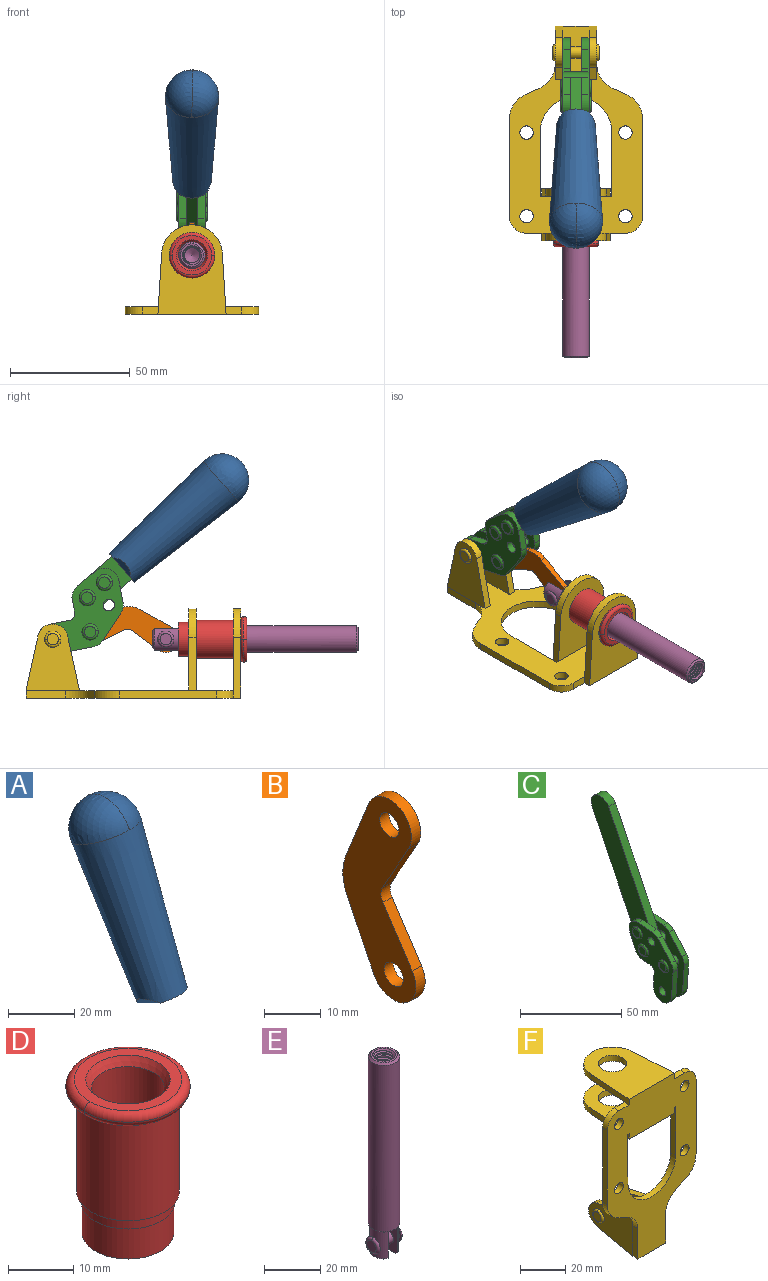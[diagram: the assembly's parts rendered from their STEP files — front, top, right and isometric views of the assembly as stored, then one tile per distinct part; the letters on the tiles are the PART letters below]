
ASSEMBLY  parts=6 mates=6
PART A: 11 faces, bbox 22.3x42.6x64.5 mm
  f0: sphere r=11.13mm, area 411.4mm2, adj f1,f8
  f1: cone r=11.11mm half-angle=3.3deg, axis (0,0.44,0.9), area 3251.8mm2, adj f0,f7,f8,f9,f10
  f2: cylinder r=6.16mm len=11.7mm, axis (1,0,0), area 89.5mm2, adj f3,f4,f5,f6
  f3: plane 60.23x36.75mm, normal (-1,0,0), area 763.6mm2, adj f2,f4,f6,f10
  f4: plane 51.37x25.05mm, normal (0,0.9,-0.44), area 264.2mm2, adj f2,f3,f5,f10
  f5: plane 60.23x36.75mm, normal (1,0,0), area 763.6mm2, adj f2,f4,f6,f10
  f6: plane 51.37x25.05mm, normal (0,-0.9,0.44), area 264.2mm2, adj f2,f3,f5,f10
  f7: plane 9.95x5.95mm, normal (0.71,-0.31,-0.64), area 25.8mm2, adj f1,f10
  f8: sphere r=11.13mm, area 411.4mm2, adj f0,f1
  f9: plane 9.95x5.95mm, normal (-0.71,-0.31,-0.64), area 25.8mm2, adj f1,f10
  f10: plane 14.27x11.38mm, normal (0,-0.44,-0.9), area 106.7mm2, adj f1,f3,f4,f5,f6,f7,f9
PART B: 12 faces, bbox 2.3x18.2x42.8 mm
  f0: cylinder r=2.4mm len=4.8mm, axis (1,0,0), area 34.9mm2, adj f4,f11
  f1: cylinder r=10.41mm len=8.47mm, axis (1,0,0), area 20.2mm2, adj f4,f9,f10,f11
  f2: cylinder r=3.05mm len=3.16mm, axis (1,0,0), area 7.7mm2, adj f4,f6,f7,f11
  f3: cylinder r=2.4mm len=4.8mm, axis (1,0,0), area 34.9mm2, adj f4,f11
  f4: plane 42.81x18.23mm, normal (-1,0,0), area 414.1mm2, adj f0,f1,f2,f3,f5,f6,f7,f8
  f5: cylinder r=5.54mm len=10.67mm, axis (1,0,0), area 41.8mm2, adj f4,f6,f10,f11
  f6: plane 11.66x6.53mm, normal (0,-0.87,-0.49), area 30.9mm2, adj f2,f4,f5,f11
  f7: plane 11.17x7.33mm, normal (0,-0.84,0.55), area 30.9mm2, adj f2,f4,f8,f11
  f8: cylinder r=5.54mm len=10.51mm, axis (1,0,0), area 41.8mm2, adj f4,f7,f9,f11
  f9: plane 13.67x6.67mm, normal (0,0.9,-0.44), area 35.1mm2, adj f1,f4,f8,f11
  f10: plane 14.1x5.7mm, normal (0,0.93,0.37), area 35.1mm2, adj f1,f4,f5,f11
  f11: plane 42.81x18.23mm, normal (1,0,0), area 414.1mm2, adj f0,f1,f2,f3,f5,f6,f7,f8
PART C: 59 faces, bbox 12.9x60.2x99.6 mm
  f0: torus R=2.39mm, axis (-1,0,0), area 14.9mm2, adj f20,f43,f51
  f1: torus R=2.39mm, axis (-1,0,0), area 14.9mm2, adj f19,f42,f51
  f2: torus R=2.39mm, axis (-1,0,0), area 14.9mm2, adj f18,f35,f51
  f3: torus R=2.39mm, axis (-1,0,0), area 14.9mm2, adj f14,f17,f23
  f4: torus R=2.39mm, axis (-1,0,0), area 14.9mm2, adj f13,f16,f23
  f5: torus R=2.39mm, axis (-1,0,0), area 14.9mm2, adj f12,f15,f23
  f6: cylinder r=2.39mm len=4.78mm, axis (1,0,0), area 46.5mm2, adj f48,f50,f51
  f7: cylinder r=2.39mm len=4.78mm, axis (1,0,0), area 46.5mm2, adj f50,f51
  f8: cylinder r=6.35mm len=12.68mm, axis (1,0,0), area 61.8mm2, adj f38,f39,f50,f51
  f9: cylinder r=2.39mm len=4.78mm, axis (-1,0,0), area 70.5mm2, adj f46,f50
  f10: cylinder r=2.39mm len=4.78mm, axis (-1,0,0), area 46.5mm2, adj f23,f45,f46
  f11: cylinder r=2.39mm len=4.78mm, axis (-1,0,0), area 46.5mm2, adj f23,f46
  f12: plane 4.78x4.78mm, normal (1,0,0), area 17.9mm2, adj f5,f15
  f13: plane 4.78x4.78mm, normal (1,0,0), area 17.9mm2, adj f4,f16
  f14: plane 4.78x4.78mm, normal (1,0,0), area 17.9mm2, adj f3,f17
  f15: torus R=2.39mm, axis (-1,0,0), area 14.9mm2, adj f5,f12,f23
  f16: torus R=2.39mm, axis (-1,0,0), area 14.9mm2, adj f4,f13,f23
  f17: torus R=2.39mm, axis (-1,0,0), area 14.9mm2, adj f3,f14,f23
  f18: plane 4.78x4.78mm, normal (-1,0,0), area 17.9mm2, adj f2,f35
  f19: plane 4.78x4.78mm, normal (-1,0,0), area 17.9mm2, adj f1,f42
  f20: plane 4.78x4.78mm, normal (-1,0,0), area 17.9mm2, adj f0,f43
  f21: plane 2.26x0.2mm, normal (1,0,0), area 0.2mm2, adj f31,f44
  f22: plane 2.26x0.2mm, normal (-1,0,0), area 0.2mm2, adj f41,f44
  f23: plane 39.37x30.77mm, normal (1,0,0), area 565.5mm2, adj f3,f4,f5,f10,f11,f15,f16,f17
  f24: cylinder r=6.1mm len=4.15mm, axis (-1,0,0), area 14.7mm2, adj f23,f25,f32,f46
  f25: plane 10.25x9.01mm, normal (0,-0.75,0.66), area 42.3mm2, adj f23,f24,f26,f46
  f26: cylinder r=6.35mm len=4.64mm, axis (-1,0,0), area 15.6mm2, adj f23,f25,f27,f46
  f27: plane 15.84x3.1mm, normal (0,-1,-0.07), area 49.2mm2, adj f23,f26,f28,f46
  f28: cylinder r=6.35mm len=12.68mm, axis (-1,0,0), area 61.8mm2, adj f23,f27,f29,f46
  f29: plane 8.11x3.1mm, normal (0,1,0.07), area 25.2mm2, adj f23,f28,f30,f46
  f30: cylinder r=3.05mm len=3.25mm, axis (-1,0,0), area 14.8mm2, adj f23,f29,f31,f46
  f31: plane 5.99x3.1mm, normal (0,0.07,-1), area 18.6mm2, adj f21,f23,f30,f44,f46
  f32: plane 9.5x3.1mm, normal (0,-0.07,1), area 29.5mm2, adj f23,f24,f33,f46,f47
  f33: cylinder r=6.1mm len=8.63mm, axis (-1,0,0), area 39.1mm2, adj f23,f32,f34,f47
  f34: plane 8.65x3.96mm, normal (0,0.91,-0.42), area 29.5mm2, adj f23,f33,f44,f47
  f35: torus R=2.39mm, axis (-1,0,0), area 14.9mm2, adj f2,f18,f51
  f36: plane 10.25x9.01mm, normal (0,-0.75,0.66), area 42.3mm2, adj f37,f49,f50,f51
  f37: cylinder r=6.35mm len=4.64mm, axis (1,0,0), area 15.6mm2, adj f36,f38,f50,f51
  f38: plane 15.84x3.1mm, normal (0,-1,-0.07), area 49.2mm2, adj f8,f37,f50,f51
  f39: plane 8.11x3.1mm, normal (0,1,0.07), area 25.2mm2, adj f8,f40,f50,f51
  f40: cylinder r=3.05mm len=3.25mm, axis (1,0,0), area 14.8mm2, adj f39,f41,f50,f51
  f41: plane 5.99x3.1mm, normal (0,0.07,-1), area 18.6mm2, adj f22,f40,f44,f50,f51
  f42: torus R=2.39mm, axis (-1,0,0), area 14.9mm2, adj f1,f19,f51
  f43: torus R=2.39mm, axis (-1,0,0), area 14.9mm2, adj f0,f20,f51
  f44: cylinder r=6.35mm len=12.12mm, axis (-1,0,0), area 128.9mm2, adj f21,f22,f23,f31,f34,f41,f46,f47
  f45: plane 2.65x1.35mm, normal (1,0,0), area 1mm2, adj f10,f55
  f46: plane 39.08x20.42mm, normal (-1,0,0), area 412.5mm2, adj f9,f10,f11,f24,f25,f26,f27,f28
  f47: plane 77.62x39.82mm, normal (1,0,0), area 850mm2, adj f32,f33,f34,f44,f53,f54,f55
  f48: plane 2.65x1.35mm, normal (-1,0,0), area 1mm2, adj f6,f55
  f49: cylinder r=6.1mm len=4.15mm, axis (1,0,0), area 14.7mm2, adj f36,f50,f51,f56
  f50: plane 39.08x20.42mm, normal (1,0,0), area 412.5mm2, adj f6,f7,f8,f9,f36,f37,f38,f39
  f51: plane 39.37x30.77mm, normal (-1,0,0), area 565.5mm2, adj f0,f1,f2,f6,f7,f8,f35,f36
  f52: plane 8.65x3.96mm, normal (0,0.91,-0.42), area 29.5mm2, adj f44,f51,f57,f58
  f53: plane 68.49x33.4mm, normal (0,0.9,-0.44), area 358.1mm2, adj f44,f47,f54,f58
  f54: cylinder r=6.35mm len=12.06mm, axis (1,0,0), area 93.7mm2, adj f47,f53,f55,f58
  f55: plane 68.49x33.4mm, normal (0,-0.9,0.44), area 358.1mm2, adj f44,f45,f46,f47,f48,f50,f54,f58
  f56: plane 9.5x3.1mm, normal (0,-0.07,1), area 29.5mm2, adj f49,f50,f51,f57,f58
  f57: cylinder r=6.1mm len=8.63mm, axis (1,0,0), area 39.1mm2, adj f51,f52,f56,f58
  f58: plane 77.62x39.82mm, normal (-1,0,0), area 850mm2, adj f44,f52,f53,f54,f55,f56,f57
PART D: 15 faces, bbox 20.6x20.6x28.7 mm
  f0: torus R=8.26mm, axis (0,0,1), area 56.8mm2, adj f1,f10,f12
  f1: torus R=8.26mm, axis (0,0,1), area 56.8mm2, adj f0,f6,f13
  f2: cylinder r=5.59mm len=25.91mm, axis (0,0,1), area 909.6mm2, adj f3,f4
  f3: cone r=6.86mm half-angle=45deg, axis (0,0,-1), area 70.2mm2, adj f2,f14
  f4: cone r=6.47mm half-angle=30deg, axis (0,0,1), area 66.7mm2, adj f2,f13
  f5: cylinder r=7.04mm len=14.07mm, axis (0,0,1), area 252.6mm2, adj f11,f14
  f6: torus R=8.26mm, axis (0,0,1), area 56.8mm2, adj f1,f12,f13
  f7: cylinder r=7.16mm len=14.33mm, axis (0,0,1), area 91.5mm2, adj f9,f11
  f8: cylinder r=7.86mm len=18.42mm, axis (0,0,1), area 909.6mm2, adj f9,f10
  f9: plane 15.72x15.72mm, normal (0,0,-1), area 33mm2, adj f7,f8
  f10: plane 16.51x16.51mm, normal (0,0,-1), area 19.9mm2, adj f0,f8,f12
  f11: plane 14.33x14.33mm, normal (0,0,-1), area 5.7mm2, adj f5,f7
  f12: torus R=8.26mm, axis (0,0,1), area 56.8mm2, adj f0,f6,f10
  f13: plane 16.51x16.51mm, normal (0,0,1), area 82.7mm2, adj f1,f4,f6
  f14: plane 14.07x14.07mm, normal (0,0,-1), area 7.8mm2, adj f3,f5
PART E: 48 faces, bbox 12.6x11.1x86.1 mm
  f0: torus R=2.41mm, axis (-1,0,0), area 15mm2, adj f30,f32,f34
  f1: torus R=2.41mm, axis (-1,0,0), area 15mm2, adj f29,f31,f33
  f2: cylinder r=5.54mm len=72.39mm, axis (0,0,1), area 2518.5mm2, adj f3,f4,f42,f43
  f3: cone r=5.54mm half-angle=45deg, axis (0,0,1), area 7.6mm2, adj f2,f5,f41
  f4: cone r=5.54mm half-angle=45deg, axis (0,0,-1), area 34.9mm2, adj f2,f39
  f5: cylinder r=5.08mm len=11.48mm, axis (0,0,1), area 108.3mm2, adj f3,f7,f8,f41
  f6: cylinder r=2.41mm len=4.83mm, axis (-1,0,0), area 71.2mm2, adj f40,f41
  f7: cylinder r=2.41mm len=4.83mm, axis (-1,0,0), area 7.6mm2, adj f5,f34
  f8: cone r=5.08mm half-angle=45deg, axis (0,0,1), area 10.6mm2, adj f5,f37,f41
  f9: cone r=3.98mm half-angle=45deg, axis (0,0,1), area 17.6mm2, adj f27,f39,f45,f46,f47
  f10: cylinder r=2.41mm len=4.83mm, axis (-1,0,0), area 7.6mm2, adj f33,f38
  f11: cylinder r=3.2mm len=6.4mm, axis (0,0,1), area 78.4mm2, adj f12,f28,f44,f45,f47
  f12: cylinder r=3.2mm len=6.4mm, axis (0,0,1), area 10.5mm2, adj f11,f13,f45,f47
  f13: cylinder r=3.2mm len=6.4mm, axis (0,0,1), area 10.5mm2, adj f12,f14,f45,f47
  f14: cylinder r=3.2mm len=6.4mm, axis (0,0,1), area 10.5mm2, adj f13,f15,f45,f47
  f15: cylinder r=3.2mm len=6.4mm, axis (0,0,1), area 10.5mm2, adj f14,f16,f45,f47
  f16: cylinder r=3.2mm len=6.4mm, axis (0,0,1), area 10.5mm2, adj f15,f17,f45,f47
  f17: cylinder r=3.2mm len=6.4mm, axis (0,0,1), area 10.5mm2, adj f16,f18,f45,f47
  f18: cylinder r=3.2mm len=6.4mm, axis (0,0,1), area 10.5mm2, adj f17,f19,f45,f47
  f19: cylinder r=3.2mm len=6.4mm, axis (0,0,1), area 10.5mm2, adj f18,f20,f45,f47
  f20: cylinder r=3.2mm len=6.4mm, axis (0,0,1), area 10.5mm2, adj f19,f21,f45,f47
  f21: cylinder r=3.2mm len=6.4mm, axis (0,0,1), area 10.5mm2, adj f20,f22,f45,f47
  f22: cylinder r=3.2mm len=6.4mm, axis (0,0,1), area 10.5mm2, adj f21,f23,f45,f47
  f23: cylinder r=3.2mm len=6.4mm, axis (0,0,1), area 10.5mm2, adj f22,f24,f45,f47
  f24: cylinder r=3.2mm len=6.4mm, axis (0,0,1), area 10.5mm2, adj f23,f25,f45,f47
  f25: cylinder r=3.2mm len=6.4mm, axis (0,0,1), area 10.5mm2, adj f24,f26,f45,f47
  f26: cylinder r=3.2mm len=6.4mm, axis (0,0,1), area 10.5mm2, adj f25,f27,f45,f47
  f27: cylinder r=3.2mm len=6.4mm, axis (0,0,1), area 7.4mm2, adj f9,f26,f45,f47
  f28: cone r=3.2mm half-angle=60deg, axis (0,0,1), area 37.2mm2, adj f11
  f29: plane 4.83x4.83mm, normal (-1,0,0), area 18.3mm2, adj f1,f31
  f30: plane 4.83x4.83mm, normal (1,0,0), area 18.3mm2, adj f0,f32
  f31: torus R=2.41mm, axis (-1,0,0), area 15mm2, adj f1,f29,f33
  f32: torus R=2.41mm, axis (-1,0,0), area 15mm2, adj f0,f30,f34
  f33: plane 6.83x6.83mm, normal (1,0,0), area 18.3mm2, adj f1,f10,f31
  f34: plane 6.83x6.83mm, normal (-1,0,0), area 18.3mm2, adj f0,f7,f32
  f35: cone r=5.08mm half-angle=45deg, axis (0,0,1), area 10.6mm2, adj f36,f38,f40
  f36: plane 7.25x1.97mm, normal (0,0,-1), area 10mm2, adj f35,f40
  f37: plane 7.25x1.97mm, normal (0,0,-1), area 10mm2, adj f8,f41
  f38: cylinder r=5.08mm len=11.48mm, axis (0,0,1), area 108.3mm2, adj f10,f35,f40,f42
  f39: plane 9.55x9.55mm, normal (0,0,1), area 22mm2, adj f4,f9
  f40: plane 12.76x10.09mm, normal (1,0,0), area 95.7mm2, adj f6,f35,f36,f38,f42,f43
  f41: plane 12.76x10.09mm, normal (-1,0,0), area 95.7mm2, adj f3,f5,f6,f8,f37,f43
  f42: cone r=5.54mm half-angle=45deg, axis (0,0,1), area 7.6mm2, adj f2,f38,f40
  f43: plane 11.07x4.7mm, normal (0,0,-1), area 50.4mm2, adj f2,f40,f41
  f44: plane 0.89x0.62mm, normal (-1,0,0), area 0.3mm2, adj f11,f45,f46,f47
  f45: bspline ~24.8x7.63mm, area 266.6mm2, adj f9,f11,f12,f13,f14,f15,f16,f17
  f46: bspline ~24.87x7.63mm, area 73.6mm2, adj f9,f44,f45,f47
  f47: bspline ~24.98x7.63mm, area 272.5mm2, adj f9,f11,f12,f13,f14,f15,f16,f17
PART F: 55 faces, bbox 55.7x37.4x89.8 mm
  f0: torus R=2.41mm, axis (-1,0,0), area 15mm2, adj f11,f15,f25
  f1: torus R=2.41mm, axis (-1,0,0), area 15mm2, adj f10,f12,f22
  f2: cylinder r=2.78mm len=5.56mm, axis (0,-1,0), area 54.2mm2, adj f30,f54
  f3: cylinder r=14.99mm len=29.97mm, axis (0,-1,0), area 145.9mm2, adj f30,f49,f53,f54
  f4: cylinder r=2.78mm len=5.56mm, axis (0,-1,0), area 54.2mm2, adj f30,f54
  f5: cylinder r=2.78mm len=5.56mm, axis (0,-1,0), area 54.2mm2, adj f30,f54
  f6: cylinder r=2.78mm len=5.56mm, axis (0,-1,0), area 54.2mm2, adj f30,f54
  f7: cylinder r=6.35mm len=12.7mm, axis (0,0,1), area 123.6mm2, adj f27,f51
  f8: cylinder r=6.35mm len=12.7mm, axis (0,0,-1), area 124.7mm2, adj f21,f35
  f9: cylinder r=2.41mm len=11.18mm, axis (-1,0,0), area 169.4mm2, adj f16,f19
  f10: plane 4.83x4.83mm, normal (1,0,0), area 18.3mm2, adj f1,f12
  f11: plane 4.83x4.83mm, normal (-1,0,0), area 18.3mm2, adj f0,f15
  f12: torus R=2.41mm, axis (-1,0,0), area 15mm2, adj f1,f10,f22
  f13: cylinder r=6.35mm len=12.41mm, axis (1,0,0), area 53.4mm2, adj f18,f19,f22,f23
  f14: cylinder r=6.35mm len=12.41mm, axis (-1,0,0), area 53.4mm2, adj f16,f17,f24,f25
  f15: torus R=2.41mm, axis (-1,0,0), area 15mm2, adj f0,f11,f25
  f16: plane 27.86x22.35mm, normal (1,0,0), area 425.4mm2, adj f9,f14,f17,f24,f30
  f17: plane 22.86x4.97mm, normal (0,0.21,0.98), area 72.5mm2, adj f14,f16,f25,f30
  f18: plane 22.86x4.97mm, normal (0,0.21,0.98), area 72.5mm2, adj f13,f19,f22,f30
  f19: plane 27.86x22.35mm, normal (-1,0,0), area 425.4mm2, adj f9,f13,f18,f23,f30
  f20: cylinder r=12.7mm len=25.35mm, axis (0,0,-1), area 119.8mm2, adj f21,f34,f35,f36
  f21: plane 34.21x28.07mm, normal (0,0,-1), area 702.4mm2, adj f8,f20,f30,f34,f36
  f22: plane 27.96x22.45mm, normal (1,0,0), area 407.2mm2, adj f1,f12,f13,f18,f23,f30,f42,f43
  f23: plane 22.86x4.97mm, normal (0,0.21,-0.98), area 72.5mm2, adj f13,f19,f22,f44
  f24: plane 22.86x4.97mm, normal (0,0.21,-0.98), area 72.5mm2, adj f14,f16,f25,f44
  f25: plane 27.86x22.35mm, normal (-1,0,0), area 407.1mm2, adj f0,f14,f15,f17,f24,f30,f45,f46
  f26: plane 3.1x0.95mm, normal (0,0,-1), area 2.7mm2, adj f30,f49,f50,f54
  f27: plane 34.21x28.07mm, normal (0,0,1), area 702.4mm2, adj f7,f28,f30,f50,f52
  f28: cylinder r=12.7mm len=25.35mm, axis (0,0,1), area 118.8mm2, adj f27,f50,f51,f52
  f29: plane 3.1x0.95mm, normal (0,0,-1), area 2.7mm2, adj f30,f52,f53,f54
  f30: plane 86.54x55.63mm, normal (0,1,0), area 2362.9mm2, adj f2,f3,f4,f5,f6,f16,f17,f18
  f31: plane 40.56x3.1mm, normal (-1,0,0), area 125.7mm2, adj f30,f32,f48,f54
  f32: cylinder r=7.11mm len=7.11mm, axis (0,-1,0), area 34.6mm2, adj f30,f31,f33,f54
  f33: plane 6.67x3.1mm, normal (0,0,1), area 20.4mm2, adj f30,f32,f34,f54
  f34: plane 25.39x3.13mm, normal (-1,0.06,0), area 79.5mm2, adj f20,f21,f33,f35,f54
  f35: plane 37.31x28.45mm, normal (0,0,1), area 789.9mm2, adj f8,f20,f34,f36,f54
  f36: plane 25.39x3.13mm, normal (1,0.06,0), area 79.5mm2, adj f20,f21,f35,f37,f54
  f37: plane 6.67x3.1mm, normal (0,0,1), area 20.4mm2, adj f30,f36,f38,f54
  f38: cylinder r=7.11mm len=7.11mm, axis (0,-1,0), area 34.6mm2, adj f30,f37,f39,f54
  f39: plane 40.56x3.1mm, normal (1,0,0), area 125.7mm2, adj f30,f38,f40,f54
  f40: cylinder r=11.18mm len=10.16mm, axis (0,-1,0), area 39.5mm2, adj f30,f39,f41,f54
  f41: plane 6.09x3.1mm, normal (0.42,0,-0.91), area 20.8mm2, adj f30,f40,f42,f54
  f42: cylinder r=11.18mm len=9.41mm, axis (0,-1,0), area 37.2mm2, adj f22,f30,f41,f43,f54
  f43: plane 16.5x3.1mm, normal (1,0,0), area 51.1mm2, adj f22,f42,f44,f54
  f44: plane 17.37x3.1mm, normal (0,0,-1), area 53.8mm2, adj f23,f24,f30,f43,f45,f54
  f45: plane 16.5x3.1mm, normal (-1,0,0), area 51.1mm2, adj f25,f44,f46,f54
  f46: cylinder r=11.18mm len=9.41mm, axis (0,-1,0), area 37.2mm2, adj f25,f30,f45,f47,f54
  f47: plane 6.09x3.1mm, normal (-0.42,0,-0.91), area 20.8mm2, adj f30,f46,f48,f54
  f48: cylinder r=11.18mm len=10.16mm, axis (0,-1,0), area 39.5mm2, adj f30,f31,f47,f54
  f49: plane 26.54x3.1mm, normal (-1,0,0), area 82.3mm2, adj f3,f26,f30,f54
  f50: plane 25.39x3.1mm, normal (1,0.06,0), area 78.8mm2, adj f26,f27,f28,f51,f54
  f51: plane 37.31x28.45mm, normal (0,0,-1), area 789.9mm2, adj f7,f28,f50,f52,f54
  f52: plane 25.39x3.1mm, normal (-1,0.06,0), area 78.8mm2, adj f27,f28,f29,f51,f54
  f53: plane 26.54x3.1mm, normal (1,0,0), area 82.3mm2, adj f3,f29,f30,f54
  f54: plane 89.66x55.63mm, normal (0,-1,0), area 2678.5mm2, adj f2,f3,f4,f5,f6,f26,f29,f31
PLACE A rot(axis=(1,0,0),75deg) t=(0,4.15,9.14)mm
PLACE B rot(axis=(1,0,0),97.5deg) t=(0,12.88,2.22)mm
PLACE C rot(axis=(1,0,0),75deg) t=(0,4.15,9.14)mm
PLACE D rot(axis=(1,0,0),90deg) t=(0,9.43,0)mm
PLACE E rot(axis=(1,0,0),90deg) t=(0,9.81,0)mm
PLACE F rot(axis=(1,0,0),90deg) t=(0,9.43,0)mm fixed
MATE fastened D.f2 <-> F.f7  axis (0,-1,0) through (0,-36.96,24.61)mm
MATE revolute F.f0 <-> C.f7  axis (-1,0,0) through (0,41.52,24.61)mm
MATE fastened A.f2 <-> C.f54  axis (1,0,0) through (0,-30.37,91.94)mm
MATE revolute B.f5 <-> E.f6  axis (1,0,0) through (0,-5.67,24.61)mm
MATE slider E.f2 <-> D.f2  axis (0,-1,0) through (0,-48.97,24.61)mm
MATE revolute B.f3 <-> C.f4  axis (1,0,0) through (0,25.94,27.64)mm
